# Revit family: QF_ELECTROLUX PROFESSIONAL_725596_RE4142FRB
name_source: partatom
category: Specialty Equipment
units: mm (PartAtom-declared; Revit-internal decimal feet)

## family parameters
Always vertical = Yes
Cut with Voids When Loaded = No
Maintain Annotation Orientation = No
Part Type = Normal
Room Calculation Point = No
Round Connector Dimension = Use Diameter
Shared = Yes
Work Plane-Based = No

## types (1)
- QF_ELECTROLUX PROFESSIONAL_725596_RE4142FRB
    Default Elevation = 0 mm  [stored 0 ft]
    Depth = 835 mm
    Feet_OS = 52 mm
    H_Door = 1597 mm  [stored 5.2395 ft]
    H_Feet = 163 mm  [stored 0.534777 ft]
    Height = 2050 mm  [stored 6.72572 ft]
    Length = 1441 mm  [stored 4.72769 ft]
    OffSet_Lat = 200 mm  [stored 0.656168 ft]
    OffSet_Rea = 300 mm
    OffSet_Up = 500 mm  [stored 1.64042 ft]

note: [stored X ft] marks values corroborated as IEEE doubles in the binary element streams (Revit-internal decimal feet)

## geometry (parser evidence)
native form markers: Blend x2, Sweep x2
no freeform markers — native parametric forms only
